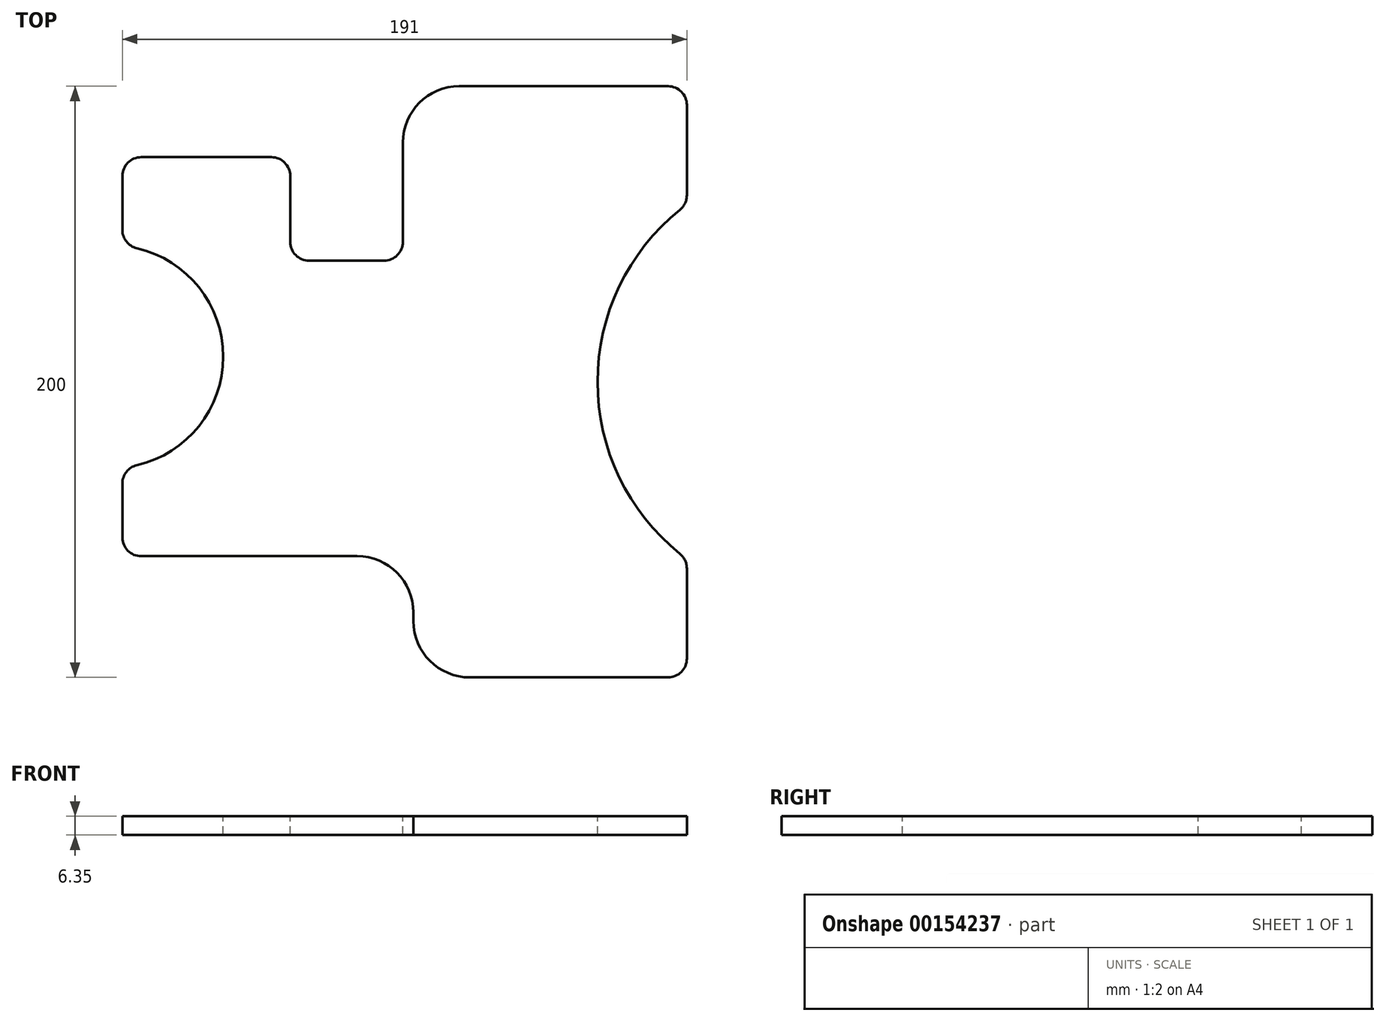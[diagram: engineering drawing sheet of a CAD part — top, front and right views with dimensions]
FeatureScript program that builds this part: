
annotation { "Feature Type Name" : "Feature", "Feature Type Description" : "" }
export const myFeature = defineFeature(function(context is Context, id is Id, definition is map)
    precondition{}
    {
        {
            var Q0;
            Q0=qCreatedBy(makeId("Top.planeOp"),FACE);
            var sketch = newSketch(context, id + "F0", { "sketchPlane" : qUnion([Q0])});
            skLineSegment(sketch, "E0", {"start": v(-92.15, -59) * mm, "end": v(-19.05, -59) * mm});
            skLineSegment(sketch, "E1", {"start": v(0, -78.05) * mm, "end": v(0, -80.95) * mm});
            skLineSegment(sketch, "E2", {"start": v(19.05, -100) * mm, "end": v(86.15, -100) * mm});
            skLineSegment(sketch, "E3", {"start": v(92.5, -93.65) * mm, "end": v(92.5, -63.12) * mm});
            skLineSegment(sketch, "E4", {"start": v(92.5, 63.12) * mm, "end": v(92.5, 93.65) * mm});
            skLineSegment(sketch, "E5", {"start": v(86.15, 100) * mm, "end": v(15.45, 100) * mm});
            skLineSegment(sketch, "E6", {"start": v(-48.05, 76) * mm, "end": v(-92.15, 76) * mm});
            skLineSegment(sketch, "E7", {"start": v(-98.5, 69.65) * mm, "end": v(-98.5, 51.39) * mm});
            skLineSegment(sketch, "E8", {"start": v(-98.5, -34.39) * mm, "end": v(-98.5, -52.65) * mm});
            skArc(sketch, "E9", {"start": v(90.13, 58.17) * mm, "mid": v(62.28, 0) * mm, "end": v(90.13, -58.17) * mm});
            skArc(sketch, "E10", {"start": v(-93.58, -28.2) * mm, "mid": v(-64.39, 8.5) * mm, "end": v(-93.58, 45.2) * mm});
            skPoint(sketch, "E11.visualSharp", {"position": v(-98.5, 76) * mm});
            skArc(sketch, "E11.filletArc", {"start": v(-92.15, 76) * mm, "mid": v(-96.64, 74.14) * mm, "end": v(-98.5, 69.65) * mm});
            skPoint(sketch, "E12.visualSharp", {"position": v(-98.5, 46) * mm});
            skArc(sketch, "E12.filletArc", {"start": v(-98.5, 51.39) * mm, "mid": v(-97.12, 47.44) * mm, "end": v(-93.58, 45.2) * mm});
            skPoint(sketch, "E13.visualSharp", {"position": v(-98.5, -29) * mm});
            skArc(sketch, "E13.filletArc", {"start": v(-93.58, -28.2) * mm, "mid": v(-97.12, -30.44) * mm, "end": v(-98.5, -34.39) * mm});
            skPoint(sketch, "E14.visualSharp", {"position": v(-98.5, -59) * mm});
            skArc(sketch, "E14.filletArc", {"start": v(-98.5, -52.65) * mm, "mid": v(-96.64, -57.14) * mm, "end": v(-92.15, -59) * mm});
            skPoint(sketch, "E15.visualSharp", {"position": v(92.5, 100) * mm});
            skArc(sketch, "E15.filletArc", {"start": v(92.5, 93.65) * mm, "mid": v(90.64, 98.14) * mm, "end": v(86.15, 100) * mm});
            skPoint(sketch, "E16.visualSharp", {"position": v(92.5, 60) * mm});
            skArc(sketch, "E16.filletArc", {"start": v(90.13, 58.17) * mm, "mid": v(91.88, 60.38) * mm, "end": v(92.5, 63.12) * mm});
            skPoint(sketch, "E17.visualSharp", {"position": v(92.5, -60) * mm});
            skArc(sketch, "E17.filletArc", {"start": v(92.5, -63.12) * mm, "mid": v(91.88, -60.38) * mm, "end": v(90.13, -58.17) * mm});
            skPoint(sketch, "E18.visualSharp", {"position": v(92.5, -100) * mm});
            skArc(sketch, "E18.filletArc", {"start": v(86.15, -100) * mm, "mid": v(90.64, -98.14) * mm, "end": v(92.5, -93.65) * mm});
            skPoint(sketch, "E19.visualSharp", {"position": v(0, 100) * mm});
            skPoint(sketch, "E20.visualSharp", {"position": v(0, -100) * mm});
            skArc(sketch, "E20.filletArc", {"start": v(0, -80.95) * mm, "mid": v(5.58, -94.42) * mm, "end": v(19.05, -100) * mm});
            skPoint(sketch, "E21.visualSharp", {"position": v(0, 76) * mm});
            skPoint(sketch, "E22.visualSharp", {"position": v(0, -59) * mm});
            skArc(sketch, "E22.filletArc", {"start": v(0, -78.05) * mm, "mid": v(-5.58, -64.58) * mm, "end": v(-19.05, -59) * mm});
            skLineSegment(sketch, "E23", {"start": v(-41.7, 69.65) * mm, "end": v(-41.7, 47.35) * mm});
            skLineSegment(sketch, "E24", {"start": v(-35.35, 41) * mm, "end": v(-9.95, 41) * mm});
            skLineSegment(sketch, "E25", {"start": v(-3.6, 47.35) * mm, "end": v(-3.6, 76) * mm});
            skLineSegment(sketch, "E26", {"start": v(-3.6, 80.95) * mm, "end": v(-3.6, 76) * mm});
            skPoint(sketch, "E27.visualSharp", {"position": v(-3.6, 100) * mm});
            skArc(sketch, "E27.filletArc", {"start": v(15.45, 100) * mm, "mid": v(1.98, 94.42) * mm, "end": v(-3.6, 80.95) * mm});
            skPoint(sketch, "E28.visualSharp", {"position": v(-41.7, 76) * mm});
            skArc(sketch, "E28.filletArc", {"start": v(-41.7, 69.65) * mm, "mid": v(-43.56, 74.14) * mm, "end": v(-48.05, 76) * mm});
            skPoint(sketch, "E29.visualSharp", {"position": v(-41.7, 41) * mm});
            skArc(sketch, "E29.filletArc", {"start": v(-41.7, 47.35) * mm, "mid": v(-39.84, 42.86) * mm, "end": v(-35.35, 41) * mm});
            skPoint(sketch, "E30.visualSharp", {"position": v(-3.6, 41) * mm});
            skArc(sketch, "E30.filletArc", {"start": v(-9.95, 41) * mm, "mid": v(-5.46, 42.86) * mm, "end": v(-3.6, 47.35) * mm});
            skSolve(sketch);
        }
        {
            var Q0;
            Q0=qSketchRegion(id+"F0",true);
            extrude(context, id + "F1", {"entities" : qUnion([Q0]), "oppositeDirection" : true, "depth" : 6.35 * mm});
        }
    });
